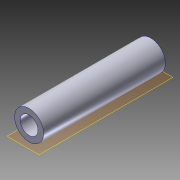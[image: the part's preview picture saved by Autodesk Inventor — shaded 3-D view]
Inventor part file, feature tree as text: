
AUTODESK INVENTOR PART (.ipt)
format: ipt  version: 2013 (Build 170138000, 138)  size: 89,600 bytes
history: native  units: mm
features: extrude x2, sketch x2, plane x1
ambient origin geometry x8: Origin, YZ Plane, XZ Plane, XY Plane, X Axis, Y Axis, Z Axis, Center Point
bodies: Solid1 (feature_tree)
feature tree (5):
  extrude  "Extrusion1"  Depth=3.0mm
  plane  "Work Plane1"
  extrude  "Extrusion2"  Depth=6.0mm
  sketch  "Sketch1"  dims[d0=4.9mm d1=3.0mm]
  sketch  "Sketch2"  dims[d2=20.5mm d3=0.0mm d4=6.0mm d6=3.0mm d7=5.0mm d8=0.5mm d9=0.0mm]
